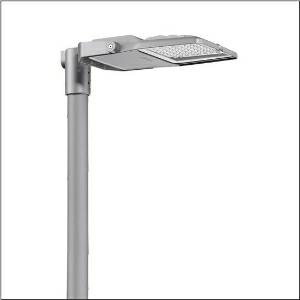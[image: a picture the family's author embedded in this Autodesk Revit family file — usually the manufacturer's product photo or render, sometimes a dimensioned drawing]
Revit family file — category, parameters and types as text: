
# Revit family: floodlight_fl_21_mini___pl43_5xa7776b2a3a_bd9b
name_source: partatom
category: Lighting Fixtures
units: mm (PartAtom-declared; Revit-internal decimal feet)

## family parameters
Cut with Voids When Loaded = No
Host = Face
Light Source = No
Part Type = Normal
Room Calculation Point = No
Round Connector Dimension = Use Diameter
Shared = No

## types (1)
- --- (1 x LED, 6390 lm, 45.7 W, 3000K)
    Apparent Load = 46 VA
    CIE Flux Codes = 27 78 99 100 100
    Color Rendering = 70
    Color Temperature = 3000K
    Default Elevation = 1800 mm
    Description = Floodlight FL 21 mini, floodlight, primary light control with lens, of PMMA, primary optical cover: protective disc, of toughened safety glass, transparent, light distribution: PL43, light emission: direct distribution, installation type: surface-mounted, LED, High Power LED, rated luminous flux: 6.390lm, luminous efficacy: 140lm/W, light colour: 730, colour temperature: 3000K, control gear: Smart Interface (Zhaga), control: flexible luminous flux parameterisation, time-dependent luminous flux control, constant luminous flux control, overheat protection, pre-setting: logarithmic dimming characteristic, with terminal, 6-pole, mains connection: 220..240V, AC, 50/60Hz, start of lifetime: 46W, end of service life: 48W, reduction: 22W, luminaire housing, of diecast aluminium, powder-coated, Siteco® metallic grey (DB 702S), corrosivity category C5 mid according to DIN EN ISO 12944, suitable for swimming pools, chlorine-resistant, sealing non-destructively replaceable, please order mast flange separately, mast bracket, of steel, galvanised, powder-coated, Siteco® metallic grey (DB 702S), Smart Interface below and above, protection rating (complete): IP66, insulation class (complete): insulation class II (safety insulation), certification: CE, ENEC, VDE, protection symbol: D, impact resistance: IK08, permissible operating ambient temperature: -40..+40°C, permissible operating ambient temperature for outdoor applications: -40..+50°C, standard: DIN EN 12944, LABS conformity tested according to VDMA 24364:2018-05, packaging unit: 1 piece

Light Distribution: PL43
    Height = 70 mm
    Lamp = 1 x LED
    Lamp Light Flux = 6390 lm
    Lamp Power = 45.7 W
    Lamp count = 1
    Length = 485 mm
    Luminous efficacy = 140 lm/W
    Manufacturer = Siteco
    ModVariant = No
    Model = 5XA7776B2A3A
    Number of Poles = 1
    OnlyDefault = Yes
    Power Factor = 1
    Product Name = Floodlight FL 21 mini | PL43
    Product group = floodlight | pylon annexe
    ProductGroupID = 6200
    Protection Class = Protection class II
    Protection Degree = IP 66
    RLX_Detail_Level = 1
    RLX_Emergency_Light_Flux = 0 lm
    RLX_Emergency_Type = 0
    RLX_Emergency_Type_DB = No
    RlxData = <blob elided: 100849 chars, md5=1eb16280>
    Socket = socket
    Standby Power = 0 W
    System Light Flux = 6390 lm
    System Power = 46 W
    Type Comments = factory setting: luminous flux: 100 % | dim-lin: 254 | 463 mA
    Type Image = l_1007125.jpg
    URL = http://relux.com
    VarID = @adj_161224
    Voltage = 0 V
    Weight = 0.00 kg
    Width = 337 mm

## geometry (parser evidence)
native form markers: Blend x4, Sweep x14
no freeform markers — native parametric forms only
